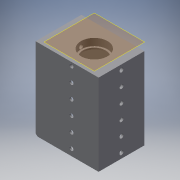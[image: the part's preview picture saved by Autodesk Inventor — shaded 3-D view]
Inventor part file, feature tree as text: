
AUTODESK INVENTOR PART (.ipt)
format: ipt  version: 2019.4 (Build 234330000, 330)  size: 218,112 bytes
history: native  units: mm
features: extrude x7, sketch x6, other x6, reference x4, projected_geometry x4, plane x3, pattern_linear x1, fillet x1
ambient origin geometry x8: Origin, YZ Plane, XZ Plane, XY Plane, X Axis, Y Axis, Z Axis, Center Point
bodies: Solid1 (feature_tree)
feature tree (32):
  plane  "Work Plane1"
  sketch  "Sketch1"  dims[d0=0.25mm d1=3.0mm]
  plane  "Work Plane2"
  extrude  "Extrusion1"  Depth=3.0mm
  plane  "Work Plane3"
  extrude  "Extrusion2"  Depth=10.0mm TaperAngle=0.0deg
  extrude  "Extrusion3"  Depth=10.0mm TaperAngle=0.0deg
  extrude  "Extrusion4"  Depth=2.8mm
  extrude  "Extrusion5"  Depth=10.0mm
  pattern_linear  "Rectangular Pattern1"  Count1=4 Spacing1=0.0mm
  fillet  "Fillet1"  Radius=10.0mm
  extrude  "Extrusion6"  Depth=1.0mm TaperAngle=0.0deg
  extrude  "Extrusion7"  Depth=1.0mm TaperAngle=0.0deg
  reference  "Reference1"
  reference  "Reference2"
  projected_geometry  "Projected Loop1"
  sketch  "Sketch3"  dims[d2=9.0mm d3=10.0mm d4=0.0mm]
  projected_geometry  "Projected Loop2"
  reference  "Reference3"
  sketch  "Sketch4"  dims[d5=0.2mm d6=10.0mm d7=0.0mm]
  reference  "Reference4"
  projected_geometry  "Projected Loop3"
  sketch  "Sketch5"  dims[d8=40.0mm d9=0.0mm d10=2.8mm]
  projected_geometry  "Projected Loop4"
  sketch  "Sketch6"  dims[d11=20.0mm d12=0.0mm d13=2.8mm d14=40.0mm d15=0.0mm d16=60.0mm d18=10.0mm]
  sketch  "Sketch7"  dims[d19=2.0mm d20=1.0mm d21=0.0mm d22=4.0mm d23=0.0mm d24=0.3mm]
  other  "<userpath>\Dropbox\cellSTORM\00_RGB_Laser_converted.iam"
  other  "00_RGB_Laser_converted.iam"
  other  "00_lens_f25mm:1"
  other  "00_RGB_Laser_Laserlands:1"
  other  "00_LASER_640nm:1"
  other  "Assembly1"
